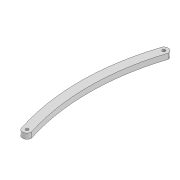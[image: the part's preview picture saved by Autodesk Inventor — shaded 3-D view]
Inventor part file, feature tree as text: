
AUTODESK INVENTOR PART (.ipt)
format: ipt  version: 2022 (Build 260153000, 153)  size: 93,184 bytes
history: native  units: mm
features: extrude x1, sketch x1
ambient origin geometry x8: Origin, YZ Plane, XZ Plane, XY Plane, X Axis, Y Axis, Z Axis, Center Point
bodies: Solid1 (feature_tree)
feature tree (2):
  extrude  "Extrusion1"  Depth=250.0mm
  sketch  "Sketch1"  dims[d0=3.3mm d1=3.3mm d2=10.0mm d3=153.584mm d6=6.0mm d7=0.0mm d12=250.0mm d13=250.0mm]
